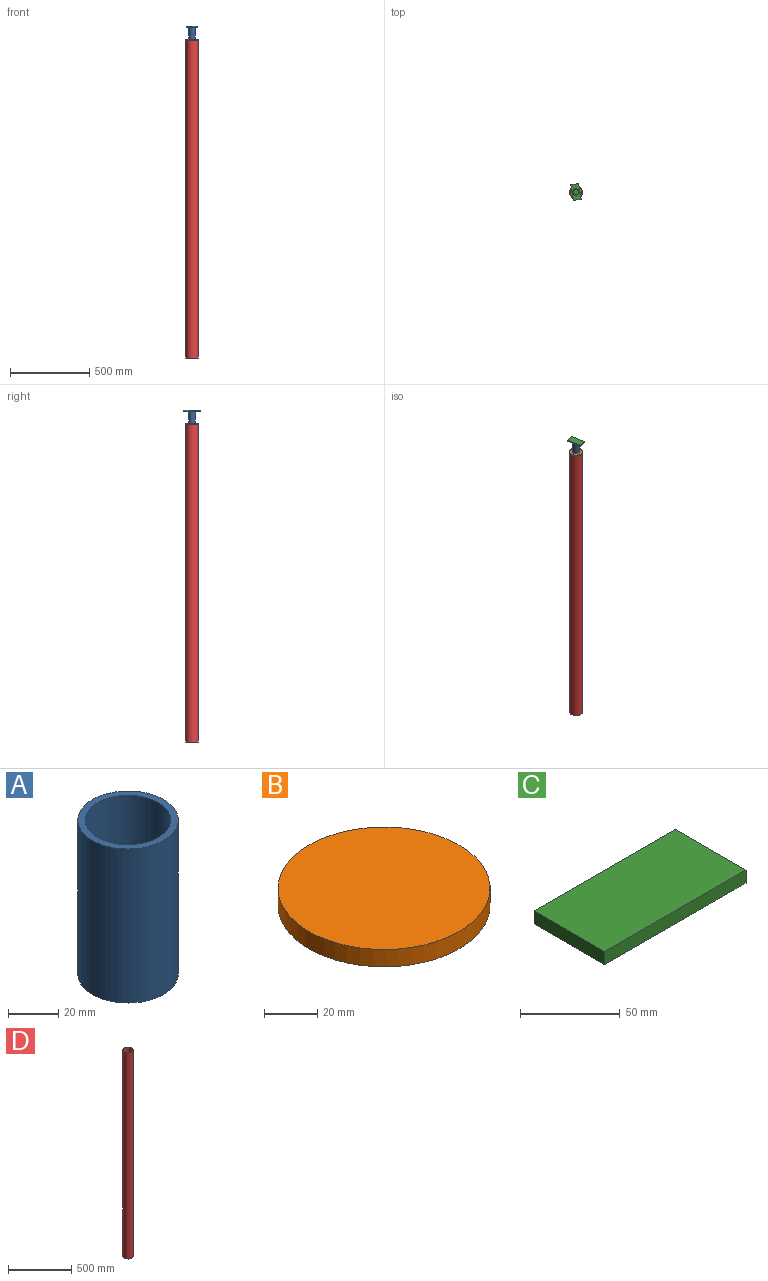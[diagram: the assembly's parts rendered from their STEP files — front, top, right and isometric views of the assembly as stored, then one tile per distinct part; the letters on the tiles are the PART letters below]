
ASSEMBLY  parts=4 mates=6
PART A: 4 faces, bbox 40x40x75 mm
  f0: cylinder r=17mm len=75mm, axis (0,0,-1), area 8011.1mm2, adj f2,f3
  f1: cylinder r=20mm len=75mm, axis (0,0,-1), area 9424.8mm2, adj f2,f3
  f2: plane 40x40mm, normal (0,0,1), area 348.7mm2, adj f0,f1
  f3: plane 40x40mm, normal (0,0,-1), area 348.7mm2, adj f0,f1
PART B: 3 faces, bbox 80x80x8 mm
  f0: cylinder r=40mm len=80mm, axis (0,0,-1), area 2010.6mm2, adj f1,f2
  f1: plane 80x80mm, normal (0,0,1), area 5026.5mm2, adj f0
  f2: plane 80x80mm, normal (0,0,-1), area 5026.5mm2, adj f0
PART C: 6 faces, bbox 100x50x8 mm
  f0: plane 50x8mm, normal (-1,0,0), area 400mm2, adj f1,f3,f4,f5
  f1: plane 100x8mm, normal (0,-1,0), area 800mm2, adj f0,f2,f4,f5
  f2: plane 50x8mm, normal (1,0,0), area 400mm2, adj f1,f3,f4,f5
  f3: plane 100x8mm, normal (0,1,0), area 800mm2, adj f0,f2,f4,f5
  f4: plane 100x50mm, normal (0,0,1), area 5000mm2, adj f0,f1,f2,f3
  f5: plane 100x50mm, normal (0,0,-1), area 5000mm2, adj f0,f1,f2,f3
PART D: 4 faces, bbox 80x80x2000 mm
  f0: cylinder r=36.4mm len=2000mm, axis (0,0,-1), area 457415.9mm2, adj f2,f3
  f1: cylinder r=40mm len=2000mm, axis (0,0,-1), area 502654.8mm2, adj f2,f3
  f2: plane 80x80mm, normal (0,0,1), area 864.1mm2, adj f0,f1
  f3: plane 80x80mm, normal (0,0,-1), area 864.1mm2, adj f0,f1
PLACE A rot(axis=(0,0,-1),133.9deg) t=(0,0,2008)mm
PLACE B rot(axis=(0.93,0.38,0),180deg) t=(0,0,2008)mm
PLACE C rot(axis=(0.77,-0.64,0),180deg) t=(15.96,53.57,2091)mm
PLACE D at identity fixed
MATE planar A.f1 <-> B.f0  axis (0,0,-1) through (0,0,2008)mm
MATE cylindrical B.f0 <-> D.f1  axis (0,0,1) through (0,0,2004)mm
MATE planar C.f4 <-> A.f1  axis (0,0,-1) through (0,0,2083)mm
MATE cylindrical A.f1 <-> D.f1  axis (0,0,-1) through (0,0,2045.5)mm
MATE planar B.f0 <-> D.f1  axis (0,0,-1) through (0,0,2000)mm
MATE cylindrical C.f5 <-> D.f1  axis (0,0,1) through (0,0,2091)mm
